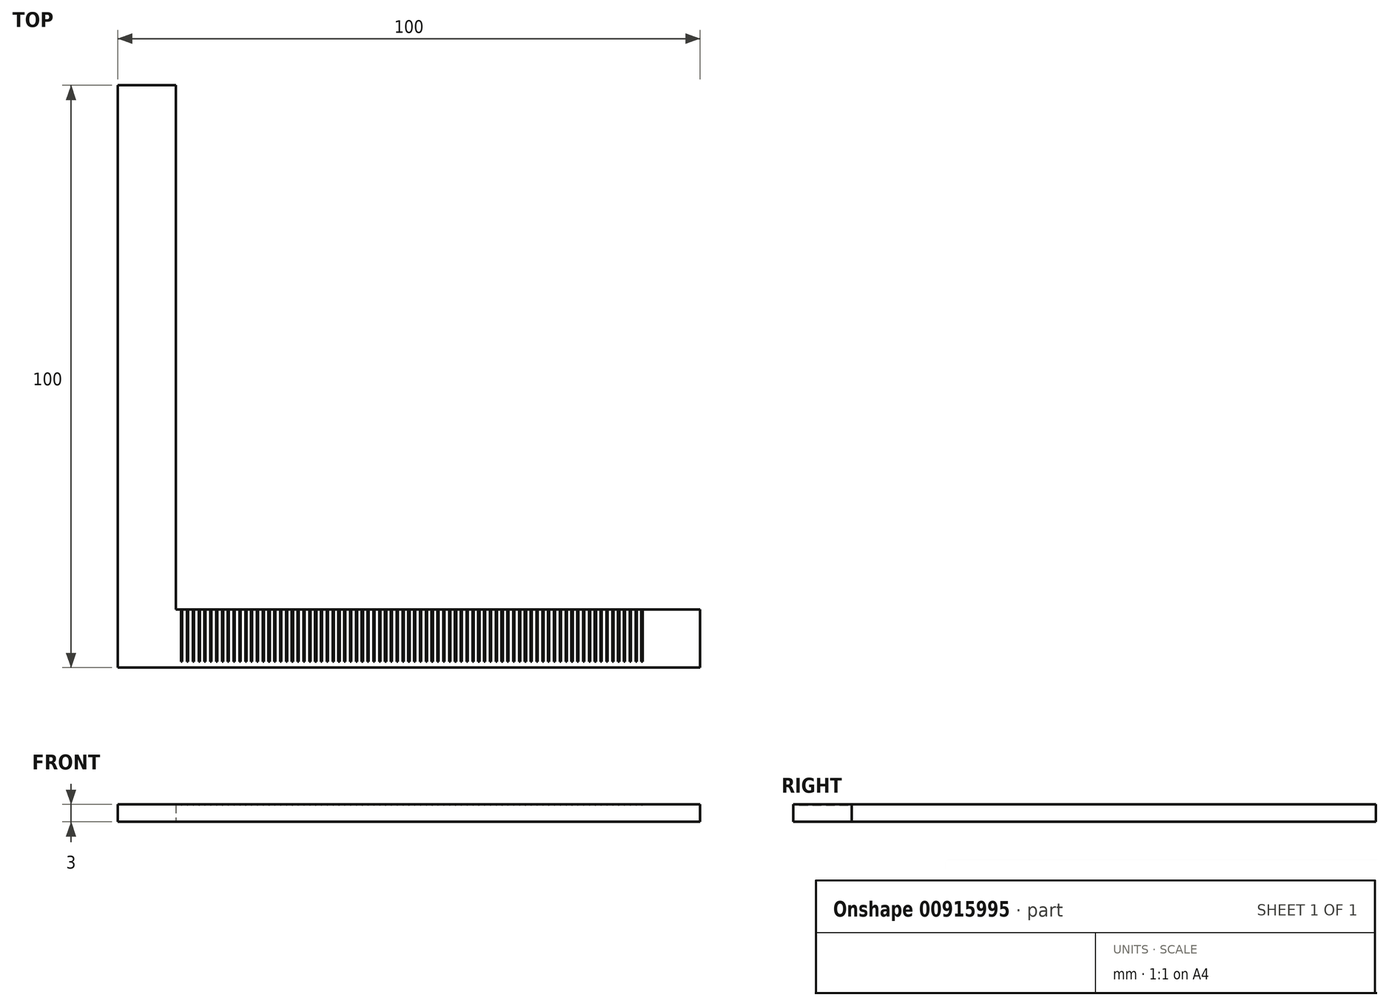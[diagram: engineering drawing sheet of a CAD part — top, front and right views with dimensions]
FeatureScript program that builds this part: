
annotation { "Feature Type Name" : "Feature", "Feature Type Description" : "" }
export const myFeature = defineFeature(function(context is Context, id is Id, definition is map)
    precondition{}
    {
        {
            var Q0;
            Q0=qCreatedBy(makeId("Top.planeOp"),FACE);
            var sketch = newSketch(context, id + "F0", { "sketchPlane" : qUnion([Q0])});
            skLineSegment(sketch, "E0", {"start": v(0, 0) * mm, "end": v(100, 0) * mm});
            skLineSegment(sketch, "E1", {"start": v(100, 0) * mm, "end": v(100, 10) * mm});
            skLineSegment(sketch, "E2", {"start": v(100, 10) * mm, "end": v(10, 10) * mm});
            skLineSegment(sketch, "E3", {"start": v(10, 10) * mm, "end": v(10, 100) * mm});
            skLineSegment(sketch, "E4", {"start": v(10, 100) * mm, "end": v(0, 100) * mm});
            skLineSegment(sketch, "E5", {"start": v(0, 100) * mm, "end": v(0, 0) * mm});
            skSolve(sketch);
        }
        {
            var Q0;
            Q0 = qSketchRegion(id + "F0", true);
            extrude(context, id + "F1", {"entities" : qUnion([Q0]), "depth" : 3 * mm, "offsetDistance" : 25 * mm});
        }
        {
            var Q0;
            Q0=makeQuery(id+"F1.opExtrude","SWEPT_FACE",FACE,{"disambiguationData":[OSD([sQuery(id+"F0.wireOp",EDGE,"E2")])]});
            var sketch = newSketch(context, id + "F2", { "sketchPlane" : qUnion([Q0])});
            skArc(sketch, "E6", {"start": v(-11.1, 3) * mm, "mid": v(-11, 2.9) * mm, "end": v(-10.9, 3) * mm});
            skLineSegment(sketch, "E7", {"start": v(-11.1, 3) * mm, "end": v(-10.9, 3) * mm});
            skArc(sketch, "E8.1.0.0", {"start": v(-12.1, 3) * mm, "mid": v(-12, 2.9) * mm, "end": v(-11.9, 3) * mm});
            skLineSegment(sketch, "E8.1.0.1", {"start": v(-12.1, 3) * mm, "end": v(-11.9, 3) * mm});
            skArc(sketch, "E8.2.0.0", {"start": v(-13.1, 3) * mm, "mid": v(-13, 2.9) * mm, "end": v(-12.9, 3) * mm});
            skLineSegment(sketch, "E8.2.0.1", {"start": v(-13.1, 3) * mm, "end": v(-12.9, 3) * mm});
            skArc(sketch, "E8.3.0.0", {"start": v(-14.1, 3) * mm, "mid": v(-14, 2.9) * mm, "end": v(-13.9, 3) * mm});
            skLineSegment(sketch, "E8.3.0.1", {"start": v(-14.1, 3) * mm, "end": v(-13.9, 3) * mm});
            skArc(sketch, "E8.4.0.0", {"start": v(-15.1, 3) * mm, "mid": v(-15, 2.9) * mm, "end": v(-14.9, 3) * mm});
            skLineSegment(sketch, "E8.4.0.1", {"start": v(-15.1, 3) * mm, "end": v(-14.9, 3) * mm});
            skArc(sketch, "E8.5.0.0", {"start": v(-16.1, 3) * mm, "mid": v(-16, 2.9) * mm, "end": v(-15.9, 3) * mm});
            skLineSegment(sketch, "E8.5.0.1", {"start": v(-16.1, 3) * mm, "end": v(-15.9, 3) * mm});
            skArc(sketch, "E8.6.0.0", {"start": v(-17.1, 3) * mm, "mid": v(-17, 2.9) * mm, "end": v(-16.9, 3) * mm});
            skLineSegment(sketch, "E8.6.0.1", {"start": v(-17.1, 3) * mm, "end": v(-16.9, 3) * mm});
            skArc(sketch, "E8.7.0.0", {"start": v(-18.1, 3) * mm, "mid": v(-18, 2.9) * mm, "end": v(-17.9, 3) * mm});
            skLineSegment(sketch, "E8.7.0.1", {"start": v(-18.1, 3) * mm, "end": v(-17.9, 3) * mm});
            skArc(sketch, "E8.8.0.0", {"start": v(-19.1, 3) * mm, "mid": v(-19, 2.9) * mm, "end": v(-18.9, 3) * mm});
            skLineSegment(sketch, "E8.8.0.1", {"start": v(-19.1, 3) * mm, "end": v(-18.9, 3) * mm});
            skArc(sketch, "E8.9.0.0", {"start": v(-20.1, 3) * mm, "mid": v(-20, 2.9) * mm, "end": v(-19.9, 3) * mm});
            skLineSegment(sketch, "E8.9.0.1", {"start": v(-20.1, 3) * mm, "end": v(-19.9, 3) * mm});
            skArc(sketch, "E8.10.0.0", {"start": v(-21.1, 3) * mm, "mid": v(-21, 2.9) * mm, "end": v(-20.9, 3) * mm});
            skLineSegment(sketch, "E8.10.0.1", {"start": v(-21.1, 3) * mm, "end": v(-20.9, 3) * mm});
            skArc(sketch, "E8.11.0.0", {"start": v(-22.1, 3) * mm, "mid": v(-22, 2.9) * mm, "end": v(-21.9, 3) * mm});
            skLineSegment(sketch, "E8.11.0.1", {"start": v(-22.1, 3) * mm, "end": v(-21.9, 3) * mm});
            skArc(sketch, "E8.12.0.0", {"start": v(-23.1, 3) * mm, "mid": v(-23, 2.9) * mm, "end": v(-22.9, 3) * mm});
            skLineSegment(sketch, "E8.12.0.1", {"start": v(-23.1, 3) * mm, "end": v(-22.9, 3) * mm});
            skArc(sketch, "E8.13.0.0", {"start": v(-24.1, 3) * mm, "mid": v(-24, 2.9) * mm, "end": v(-23.9, 3) * mm});
            skLineSegment(sketch, "E8.13.0.1", {"start": v(-24.1, 3) * mm, "end": v(-23.9, 3) * mm});
            skArc(sketch, "E8.14.0.0", {"start": v(-25.1, 3) * mm, "mid": v(-25, 2.9) * mm, "end": v(-24.9, 3) * mm});
            skLineSegment(sketch, "E8.14.0.1", {"start": v(-25.1, 3) * mm, "end": v(-24.9, 3) * mm});
            skArc(sketch, "E8.15.0.0", {"start": v(-26.1, 3) * mm, "mid": v(-26, 2.9) * mm, "end": v(-25.9, 3) * mm});
            skLineSegment(sketch, "E8.15.0.1", {"start": v(-26.1, 3) * mm, "end": v(-25.9, 3) * mm});
            skArc(sketch, "E8.16.0.0", {"start": v(-27.1, 3) * mm, "mid": v(-27, 2.9) * mm, "end": v(-26.9, 3) * mm});
            skLineSegment(sketch, "E8.16.0.1", {"start": v(-27.1, 3) * mm, "end": v(-26.9, 3) * mm});
            skArc(sketch, "E8.17.0.0", {"start": v(-28.1, 3) * mm, "mid": v(-28, 2.9) * mm, "end": v(-27.9, 3) * mm});
            skLineSegment(sketch, "E8.17.0.1", {"start": v(-28.1, 3) * mm, "end": v(-27.9, 3) * mm});
            skArc(sketch, "E8.18.0.0", {"start": v(-29.1, 3) * mm, "mid": v(-29, 2.9) * mm, "end": v(-28.9, 3) * mm});
            skLineSegment(sketch, "E8.18.0.1", {"start": v(-29.1, 3) * mm, "end": v(-28.9, 3) * mm});
            skArc(sketch, "E8.19.0.0", {"start": v(-30.1, 3) * mm, "mid": v(-30, 2.9) * mm, "end": v(-29.9, 3) * mm});
            skLineSegment(sketch, "E8.19.0.1", {"start": v(-30.1, 3) * mm, "end": v(-29.9, 3) * mm});
            skArc(sketch, "E8.20.0.0", {"start": v(-31.1, 3) * mm, "mid": v(-31, 2.9) * mm, "end": v(-30.9, 3) * mm});
            skLineSegment(sketch, "E8.20.0.1", {"start": v(-31.1, 3) * mm, "end": v(-30.9, 3) * mm});
            skArc(sketch, "E8.21.0.0", {"start": v(-32.1, 3) * mm, "mid": v(-32, 2.9) * mm, "end": v(-31.9, 3) * mm});
            skLineSegment(sketch, "E8.21.0.1", {"start": v(-32.1, 3) * mm, "end": v(-31.9, 3) * mm});
            skArc(sketch, "E8.22.0.0", {"start": v(-33.1, 3) * mm, "mid": v(-33, 2.9) * mm, "end": v(-32.9, 3) * mm});
            skLineSegment(sketch, "E8.22.0.1", {"start": v(-33.1, 3) * mm, "end": v(-32.9, 3) * mm});
            skArc(sketch, "E8.23.0.0", {"start": v(-34.1, 3) * mm, "mid": v(-34, 2.9) * mm, "end": v(-33.9, 3) * mm});
            skLineSegment(sketch, "E8.23.0.1", {"start": v(-34.1, 3) * mm, "end": v(-33.9, 3) * mm});
            skArc(sketch, "E8.24.0.0", {"start": v(-35.1, 3) * mm, "mid": v(-35, 2.9) * mm, "end": v(-34.9, 3) * mm});
            skLineSegment(sketch, "E8.24.0.1", {"start": v(-35.1, 3) * mm, "end": v(-34.9, 3) * mm});
            skArc(sketch, "E8.25.0.0", {"start": v(-36.1, 3) * mm, "mid": v(-36, 2.9) * mm, "end": v(-35.9, 3) * mm});
            skLineSegment(sketch, "E8.25.0.1", {"start": v(-36.1, 3) * mm, "end": v(-35.9, 3) * mm});
            skArc(sketch, "E8.26.0.0", {"start": v(-37.1, 3) * mm, "mid": v(-37, 2.9) * mm, "end": v(-36.9, 3) * mm});
            skLineSegment(sketch, "E8.26.0.1", {"start": v(-37.1, 3) * mm, "end": v(-36.9, 3) * mm});
            skArc(sketch, "E8.27.0.0", {"start": v(-38.1, 3) * mm, "mid": v(-38, 2.9) * mm, "end": v(-37.9, 3) * mm});
            skLineSegment(sketch, "E8.27.0.1", {"start": v(-38.1, 3) * mm, "end": v(-37.9, 3) * mm});
            skArc(sketch, "E8.28.0.0", {"start": v(-39.1, 3) * mm, "mid": v(-39, 2.9) * mm, "end": v(-38.9, 3) * mm});
            skLineSegment(sketch, "E8.28.0.1", {"start": v(-39.1, 3) * mm, "end": v(-38.9, 3) * mm});
            skArc(sketch, "E8.29.0.0", {"start": v(-40.1, 3) * mm, "mid": v(-40, 2.9) * mm, "end": v(-39.9, 3) * mm});
            skLineSegment(sketch, "E8.29.0.1", {"start": v(-40.1, 3) * mm, "end": v(-39.9, 3) * mm});
            skArc(sketch, "E8.30.0.0", {"start": v(-41.1, 3) * mm, "mid": v(-41, 2.9) * mm, "end": v(-40.9, 3) * mm});
            skLineSegment(sketch, "E8.30.0.1", {"start": v(-41.1, 3) * mm, "end": v(-40.9, 3) * mm});
            skArc(sketch, "E8.31.0.0", {"start": v(-42.1, 3) * mm, "mid": v(-42, 2.9) * mm, "end": v(-41.9, 3) * mm});
            skLineSegment(sketch, "E8.31.0.1", {"start": v(-42.1, 3) * mm, "end": v(-41.9, 3) * mm});
            skArc(sketch, "E8.32.0.0", {"start": v(-43.1, 3) * mm, "mid": v(-43, 2.9) * mm, "end": v(-42.9, 3) * mm});
            skLineSegment(sketch, "E8.32.0.1", {"start": v(-43.1, 3) * mm, "end": v(-42.9, 3) * mm});
            skArc(sketch, "E8.33.0.0", {"start": v(-44.1, 3) * mm, "mid": v(-44, 2.9) * mm, "end": v(-43.9, 3) * mm});
            skLineSegment(sketch, "E8.33.0.1", {"start": v(-44.1, 3) * mm, "end": v(-43.9, 3) * mm});
            skArc(sketch, "E8.34.0.0", {"start": v(-45.1, 3) * mm, "mid": v(-45, 2.9) * mm, "end": v(-44.9, 3) * mm});
            skLineSegment(sketch, "E8.34.0.1", {"start": v(-45.1, 3) * mm, "end": v(-44.9, 3) * mm});
            skArc(sketch, "E8.35.0.0", {"start": v(-46.1, 3) * mm, "mid": v(-46, 2.9) * mm, "end": v(-45.9, 3) * mm});
            skLineSegment(sketch, "E8.35.0.1", {"start": v(-46.1, 3) * mm, "end": v(-45.9, 3) * mm});
            skArc(sketch, "E8.36.0.0", {"start": v(-47.1, 3) * mm, "mid": v(-47, 2.9) * mm, "end": v(-46.9, 3) * mm});
            skLineSegment(sketch, "E8.36.0.1", {"start": v(-47.1, 3) * mm, "end": v(-46.9, 3) * mm});
            skArc(sketch, "E8.37.0.0", {"start": v(-48.1, 3) * mm, "mid": v(-48, 2.9) * mm, "end": v(-47.9, 3) * mm});
            skLineSegment(sketch, "E8.37.0.1", {"start": v(-48.1, 3) * mm, "end": v(-47.9, 3) * mm});
            skArc(sketch, "E8.38.0.0", {"start": v(-49.1, 3) * mm, "mid": v(-49, 2.9) * mm, "end": v(-48.9, 3) * mm});
            skLineSegment(sketch, "E8.38.0.1", {"start": v(-49.1, 3) * mm, "end": v(-48.9, 3) * mm});
            skArc(sketch, "E8.39.0.0", {"start": v(-50.1, 3) * mm, "mid": v(-50, 2.9) * mm, "end": v(-49.9, 3) * mm});
            skLineSegment(sketch, "E8.39.0.1", {"start": v(-50.1, 3) * mm, "end": v(-49.9, 3) * mm});
            skArc(sketch, "E8.40.0.0", {"start": v(-51.1, 3) * mm, "mid": v(-51, 2.9) * mm, "end": v(-50.9, 3) * mm});
            skLineSegment(sketch, "E8.40.0.1", {"start": v(-51.1, 3) * mm, "end": v(-50.9, 3) * mm});
            skArc(sketch, "E8.41.0.0", {"start": v(-52.1, 3) * mm, "mid": v(-52, 2.9) * mm, "end": v(-51.9, 3) * mm});
            skLineSegment(sketch, "E8.41.0.1", {"start": v(-52.1, 3) * mm, "end": v(-51.9, 3) * mm});
            skArc(sketch, "E8.42.0.0", {"start": v(-53.1, 3) * mm, "mid": v(-53, 2.9) * mm, "end": v(-52.9, 3) * mm});
            skLineSegment(sketch, "E8.42.0.1", {"start": v(-53.1, 3) * mm, "end": v(-52.9, 3) * mm});
            skArc(sketch, "E8.43.0.0", {"start": v(-54.1, 3) * mm, "mid": v(-54, 2.9) * mm, "end": v(-53.9, 3) * mm});
            skLineSegment(sketch, "E8.43.0.1", {"start": v(-54.1, 3) * mm, "end": v(-53.9, 3) * mm});
            skArc(sketch, "E8.44.0.0", {"start": v(-55.1, 3) * mm, "mid": v(-55, 2.9) * mm, "end": v(-54.9, 3) * mm});
            skLineSegment(sketch, "E8.44.0.1", {"start": v(-55.1, 3) * mm, "end": v(-54.9, 3) * mm});
            skArc(sketch, "E8.45.0.0", {"start": v(-56.1, 3) * mm, "mid": v(-56, 2.9) * mm, "end": v(-55.9, 3) * mm});
            skLineSegment(sketch, "E8.45.0.1", {"start": v(-56.1, 3) * mm, "end": v(-55.9, 3) * mm});
            skArc(sketch, "E8.46.0.0", {"start": v(-57.1, 3) * mm, "mid": v(-57, 2.9) * mm, "end": v(-56.9, 3) * mm});
            skLineSegment(sketch, "E8.46.0.1", {"start": v(-57.1, 3) * mm, "end": v(-56.9, 3) * mm});
            skArc(sketch, "E8.47.0.0", {"start": v(-58.1, 3) * mm, "mid": v(-58, 2.9) * mm, "end": v(-57.9, 3) * mm});
            skLineSegment(sketch, "E8.47.0.1", {"start": v(-58.1, 3) * mm, "end": v(-57.9, 3) * mm});
            skArc(sketch, "E8.48.0.0", {"start": v(-59.1, 3) * mm, "mid": v(-59, 2.9) * mm, "end": v(-58.9, 3) * mm});
            skLineSegment(sketch, "E8.48.0.1", {"start": v(-59.1, 3) * mm, "end": v(-58.9, 3) * mm});
            skArc(sketch, "E8.49.0.0", {"start": v(-60.1, 3) * mm, "mid": v(-60, 2.9) * mm, "end": v(-59.9, 3) * mm});
            skLineSegment(sketch, "E8.49.0.1", {"start": v(-60.1, 3) * mm, "end": v(-59.9, 3) * mm});
            skArc(sketch, "E8.50.0.0", {"start": v(-61.1, 3) * mm, "mid": v(-61, 2.9) * mm, "end": v(-60.9, 3) * mm});
            skLineSegment(sketch, "E8.50.0.1", {"start": v(-61.1, 3) * mm, "end": v(-60.9, 3) * mm});
            skArc(sketch, "E8.51.0.0", {"start": v(-62.1, 3) * mm, "mid": v(-62, 2.9) * mm, "end": v(-61.9, 3) * mm});
            skLineSegment(sketch, "E8.51.0.1", {"start": v(-62.1, 3) * mm, "end": v(-61.9, 3) * mm});
            skArc(sketch, "E8.52.0.0", {"start": v(-63.1, 3) * mm, "mid": v(-63, 2.9) * mm, "end": v(-62.9, 3) * mm});
            skLineSegment(sketch, "E8.52.0.1", {"start": v(-63.1, 3) * mm, "end": v(-62.9, 3) * mm});
            skArc(sketch, "E8.53.0.0", {"start": v(-64.1, 3) * mm, "mid": v(-64, 2.9) * mm, "end": v(-63.9, 3) * mm});
            skLineSegment(sketch, "E8.53.0.1", {"start": v(-64.1, 3) * mm, "end": v(-63.9, 3) * mm});
            skArc(sketch, "E8.54.0.0", {"start": v(-65.1, 3) * mm, "mid": v(-65, 2.9) * mm, "end": v(-64.9, 3) * mm});
            skLineSegment(sketch, "E8.54.0.1", {"start": v(-65.1, 3) * mm, "end": v(-64.9, 3) * mm});
            skArc(sketch, "E8.55.0.0", {"start": v(-66.1, 3) * mm, "mid": v(-66, 2.9) * mm, "end": v(-65.9, 3) * mm});
            skLineSegment(sketch, "E8.55.0.1", {"start": v(-66.1, 3) * mm, "end": v(-65.9, 3) * mm});
            skArc(sketch, "E8.56.0.0", {"start": v(-67.1, 3) * mm, "mid": v(-67, 2.9) * mm, "end": v(-66.9, 3) * mm});
            skLineSegment(sketch, "E8.56.0.1", {"start": v(-67.1, 3) * mm, "end": v(-66.9, 3) * mm});
            skArc(sketch, "E8.57.0.0", {"start": v(-68.1, 3) * mm, "mid": v(-68, 2.9) * mm, "end": v(-67.9, 3) * mm});
            skLineSegment(sketch, "E8.57.0.1", {"start": v(-68.1, 3) * mm, "end": v(-67.9, 3) * mm});
            skArc(sketch, "E8.58.0.0", {"start": v(-69.1, 3) * mm, "mid": v(-69, 2.9) * mm, "end": v(-68.9, 3) * mm});
            skLineSegment(sketch, "E8.58.0.1", {"start": v(-69.1, 3) * mm, "end": v(-68.9, 3) * mm});
            skArc(sketch, "E8.59.0.0", {"start": v(-70.1, 3) * mm, "mid": v(-70, 2.9) * mm, "end": v(-69.9, 3) * mm});
            skLineSegment(sketch, "E8.59.0.1", {"start": v(-70.1, 3) * mm, "end": v(-69.9, 3) * mm});
            skArc(sketch, "E8.60.0.0", {"start": v(-71.1, 3) * mm, "mid": v(-71, 2.9) * mm, "end": v(-70.9, 3) * mm});
            skLineSegment(sketch, "E8.60.0.1", {"start": v(-71.1, 3) * mm, "end": v(-70.9, 3) * mm});
            skArc(sketch, "E8.61.0.0", {"start": v(-72.1, 3) * mm, "mid": v(-72, 2.9) * mm, "end": v(-71.9, 3) * mm});
            skLineSegment(sketch, "E8.61.0.1", {"start": v(-72.1, 3) * mm, "end": v(-71.9, 3) * mm});
            skArc(sketch, "E8.62.0.0", {"start": v(-73.1, 3) * mm, "mid": v(-73, 2.9) * mm, "end": v(-72.9, 3) * mm});
            skLineSegment(sketch, "E8.62.0.1", {"start": v(-73.1, 3) * mm, "end": v(-72.9, 3) * mm});
            skArc(sketch, "E8.63.0.0", {"start": v(-74.1, 3) * mm, "mid": v(-74, 2.9) * mm, "end": v(-73.9, 3) * mm});
            skLineSegment(sketch, "E8.63.0.1", {"start": v(-74.1, 3) * mm, "end": v(-73.9, 3) * mm});
            skArc(sketch, "E8.64.0.0", {"start": v(-75.1, 3) * mm, "mid": v(-75, 2.9) * mm, "end": v(-74.9, 3) * mm});
            skLineSegment(sketch, "E8.64.0.1", {"start": v(-75.1, 3) * mm, "end": v(-74.9, 3) * mm});
            skArc(sketch, "E8.65.0.0", {"start": v(-76.1, 3) * mm, "mid": v(-76, 2.9) * mm, "end": v(-75.9, 3) * mm});
            skLineSegment(sketch, "E8.65.0.1", {"start": v(-76.1, 3) * mm, "end": v(-75.9, 3) * mm});
            skArc(sketch, "E8.66.0.0", {"start": v(-77.1, 3) * mm, "mid": v(-77, 2.9) * mm, "end": v(-76.9, 3) * mm});
            skLineSegment(sketch, "E8.66.0.1", {"start": v(-77.1, 3) * mm, "end": v(-76.9, 3) * mm});
            skArc(sketch, "E8.67.0.0", {"start": v(-78.1, 3) * mm, "mid": v(-78, 2.9) * mm, "end": v(-77.9, 3) * mm});
            skLineSegment(sketch, "E8.67.0.1", {"start": v(-78.1, 3) * mm, "end": v(-77.9, 3) * mm});
            skArc(sketch, "E8.68.0.0", {"start": v(-79.1, 3) * mm, "mid": v(-79, 2.9) * mm, "end": v(-78.9, 3) * mm});
            skLineSegment(sketch, "E8.68.0.1", {"start": v(-79.1, 3) * mm, "end": v(-78.9, 3) * mm});
            skArc(sketch, "E8.69.0.0", {"start": v(-80.1, 3) * mm, "mid": v(-80, 2.9) * mm, "end": v(-79.9, 3) * mm});
            skLineSegment(sketch, "E8.69.0.1", {"start": v(-80.1, 3) * mm, "end": v(-79.9, 3) * mm});
            skArc(sketch, "E8.70.0.0", {"start": v(-81.1, 3) * mm, "mid": v(-81, 2.9) * mm, "end": v(-80.9, 3) * mm});
            skLineSegment(sketch, "E8.70.0.1", {"start": v(-81.1, 3) * mm, "end": v(-80.9, 3) * mm});
            skArc(sketch, "E8.71.0.0", {"start": v(-82.1, 3) * mm, "mid": v(-82, 2.9) * mm, "end": v(-81.9, 3) * mm});
            skLineSegment(sketch, "E8.71.0.1", {"start": v(-82.1, 3) * mm, "end": v(-81.9, 3) * mm});
            skArc(sketch, "E8.72.0.0", {"start": v(-83.1, 3) * mm, "mid": v(-83, 2.9) * mm, "end": v(-82.9, 3) * mm});
            skLineSegment(sketch, "E8.72.0.1", {"start": v(-83.1, 3) * mm, "end": v(-82.9, 3) * mm});
            skArc(sketch, "E8.73.0.0", {"start": v(-84.1, 3) * mm, "mid": v(-84, 2.9) * mm, "end": v(-83.9, 3) * mm});
            skLineSegment(sketch, "E8.73.0.1", {"start": v(-84.1, 3) * mm, "end": v(-83.9, 3) * mm});
            skArc(sketch, "E8.74.0.0", {"start": v(-85.1, 3) * mm, "mid": v(-85, 2.9) * mm, "end": v(-84.9, 3) * mm});
            skLineSegment(sketch, "E8.74.0.1", {"start": v(-85.1, 3) * mm, "end": v(-84.9, 3) * mm});
            skArc(sketch, "E8.75.0.0", {"start": v(-86.1, 3) * mm, "mid": v(-86, 2.9) * mm, "end": v(-85.9, 3) * mm});
            skLineSegment(sketch, "E8.75.0.1", {"start": v(-86.1, 3) * mm, "end": v(-85.9, 3) * mm});
            skArc(sketch, "E8.76.0.0", {"start": v(-87.1, 3) * mm, "mid": v(-87, 2.9) * mm, "end": v(-86.9, 3) * mm});
            skLineSegment(sketch, "E8.76.0.1", {"start": v(-87.1, 3) * mm, "end": v(-86.9, 3) * mm});
            skArc(sketch, "E8.77.0.0", {"start": v(-88.1, 3) * mm, "mid": v(-88, 2.9) * mm, "end": v(-87.9, 3) * mm});
            skLineSegment(sketch, "E8.77.0.1", {"start": v(-88.1, 3) * mm, "end": v(-87.9, 3) * mm});
            skArc(sketch, "E8.78.0.0", {"start": v(-89.1, 3) * mm, "mid": v(-89, 2.9) * mm, "end": v(-88.9, 3) * mm});
            skLineSegment(sketch, "E8.78.0.1", {"start": v(-89.1, 3) * mm, "end": v(-88.9, 3) * mm});
            skArc(sketch, "E8.79.0.0", {"start": v(-90.1, 3) * mm, "mid": v(-90, 2.9) * mm, "end": v(-89.9, 3) * mm});
            skLineSegment(sketch, "E8.79.0.1", {"start": v(-90.1, 3) * mm, "end": v(-89.9, 3) * mm});
            skLineSegment(sketch, "E8.direction1", {"start": v(-11.1, 3) * mm, "end": v(-12.1, 3) * mm, "construction": true});
            skSolve(sketch);
        }
        {
            var Q0;
            Q0 = qSketchRegion(id + "F2", true);
            extrude(context, id + "F3", {"entities" : qUnion([Q0]), "operationType" : NewBodyOperationType.REMOVE, "endBound" : BoundingType.UP_TO_NEXT, "oppositeDirection" : true, "depth" : 25 * mm, "hasOffset" : true, "offsetDistance" : 1 * mm});
        }
    });
